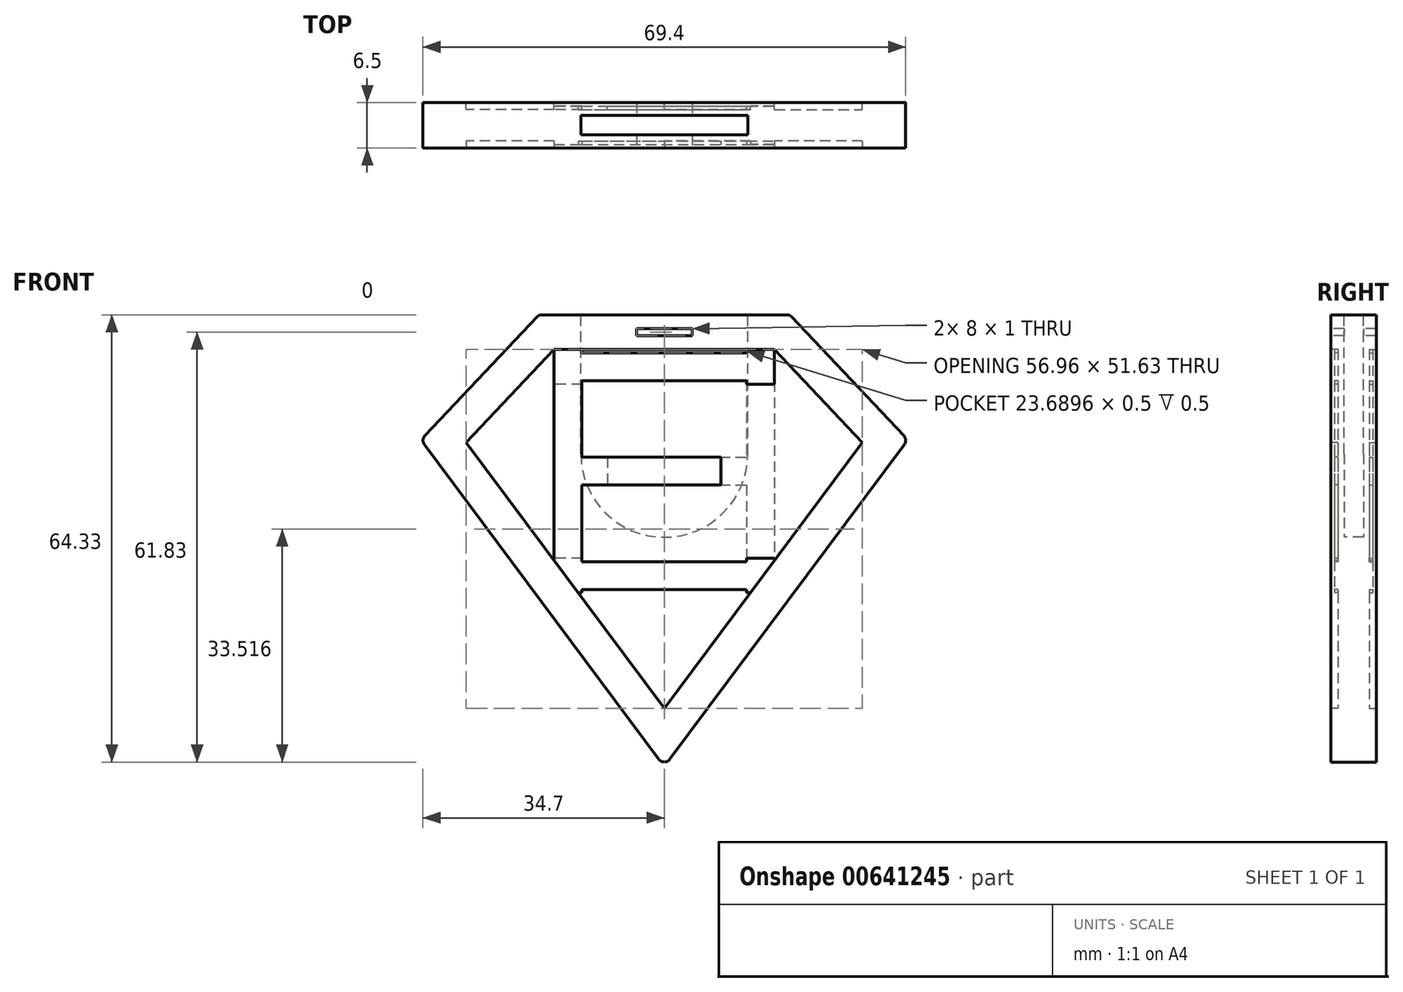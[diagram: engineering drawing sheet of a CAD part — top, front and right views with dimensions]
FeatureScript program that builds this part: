
annotation { "Feature Type Name" : "Feature", "Feature Type Description" : "" }
export const myFeature = defineFeature(function(context is Context, id is Id, definition is map)
    precondition{}
    {
        {
            var Q0;
            Q0=qCreatedBy(makeId("Front.planeOp"),FACE);
            var sketch = newSketch(context, id + "F0", { "sketchPlane" : qUnion([Q0])});
            skLineSegment(sketch, "E0", {"start": v(0, 18) * mm, "end": v(18, 18) * mm});
            skLineSegment(sketch, "E1", {"start": v(18, 18) * mm, "end": v(35, 0) * mm});
            skLineSegment(sketch, "E2", {"start": v(35, 0) * mm, "end": v(0, -47) * mm});
            skLineSegment(sketch, "E3", {"start": v(0, 18) * mm, "end": v(0, -47) * mm, "construction": true});
            skLineSegment(sketch, "E4.MirrorCS", {"start": v(-35, 0) * mm, "end": v(0, -47) * mm});
            skLineSegment(sketch, "E5.MirrorCS", {"start": v(-18, 18) * mm, "end": v(-35, 0) * mm});
            skLineSegment(sketch, "E6.MirrorCS", {"start": v(0, 18) * mm, "end": v(-18, 18) * mm});
            skSolve(sketch);
        }
        {
            var Q0;
            Q0=qSketchRegion(id+"F0",true);
            extrude(context, id + "F1", {"entities" : qUnion([Q0]), "endBound" : BoundingType.SYMMETRIC, "depth" : 6.5 * mm, "offsetDistance" : 25 * mm});
        }
        {
            var Q0;
            Q0=makeQuery(id+"F1.opExtrude","CAP_FACE",FACE,{"disambiguationData":[OSD([sQuery(id+"F0.wireOp",EDGE,"E0"),sQuery(id+"F0.wireOp",EDGE,"E1"),sQuery(id+"F0.wireOp",EDGE,"E2"),sQuery(id+"F0.wireOp",EDGE,"E4.MirrorCS"),sQuery(id+"F0.wireOp",EDGE,"E5.MirrorCS"),sQuery(id+"F0.wireOp",EDGE,"E6.MirrorCS")])],"isStart":false});
            var sketch = newSketch(context, id + "F2", { "sketchPlane" : qUnion([Q0])});
            skLineSegment(sketch, "E7.0", {"start": v(-15.84, 13) * mm, "end": v(15.84, 13) * mm});
            skLineSegment(sketch, "E8.0", {"start": v(-15.84, 13) * mm, "end": v(-28.48, -0.38) * mm});
            skLineSegment(sketch, "E9.0", {"start": v(-28.48, -0.38) * mm, "end": v(0, -38.63) * mm});
            skLineSegment(sketch, "E10.0", {"start": v(28.48, -0.38) * mm, "end": v(0, -38.63) * mm});
            skLineSegment(sketch, "E11.0", {"start": v(15.84, 13) * mm, "end": v(28.48, -0.38) * mm});
            skSolve(sketch);
        }
        {
            var Q0;
            Q0=qSketchRegion(id+"F2",true);
            extrude(context, id + "F3", {"entities" : qUnion([Q0]), "operationType" : NewBodyOperationType.REMOVE, "oppositeDirection" : true, "depth" : 0.5 * mm, "offsetDistance" : 25 * mm});
        }
        {
            var Q0;
            Q0=makeQuery(id+"F1.opExtrude","CAP_FACE",FACE,{"disambiguationData":[OSD([sQuery(id+"F0.wireOp",EDGE,"E0"),sQuery(id+"F0.wireOp",EDGE,"E1"),sQuery(id+"F0.wireOp",EDGE,"E2"),sQuery(id+"F0.wireOp",EDGE,"E4.MirrorCS"),sQuery(id+"F0.wireOp",EDGE,"E5.MirrorCS"),sQuery(id+"F0.wireOp",EDGE,"E6.MirrorCS")])],"isStart":true});
            var sketch = newSketch(context, id + "F4", { "sketchPlane" : qUnion([Q0])});
            skLineSegment(sketch, "E12.0", {"start": v(15.84, 13) * mm, "end": v(-15.84, 13) * mm});
            skLineSegment(sketch, "E13.0", {"start": v(15.84, 13) * mm, "end": v(28.48, -0.38) * mm});
            skLineSegment(sketch, "E14.0", {"start": v(28.48, -0.38) * mm, "end": v(0, -38.63) * mm});
            skLineSegment(sketch, "E15.0", {"start": v(-28.48, -0.38) * mm, "end": v(0, -38.63) * mm});
            skLineSegment(sketch, "E15.1", {"start": v(-15.84, 13) * mm, "end": v(-28.48, -0.38) * mm});
            skSolve(sketch);
        }
        {
            var Q0;
            Q0=qSketchRegion(id+"F4",true);
            extrude(context, id + "F5", {"entities" : qUnion([Q0]), "operationType" : NewBodyOperationType.REMOVE, "oppositeDirection" : true, "depth" : 0.5 * mm, "offsetDistance" : 25 * mm});
        }
        {
            var Q0;
            Q0=makeQuery(id+"F3.boolean.opBoolean","COPY",FACE,{"derivedFrom":makeQuery(id+"F3.opExtrude","CAP_FACE",FACE,{"disambiguationData":[OSD([sQuery(id+"F2.wireOp",EDGE,"E7.0"),sQuery(id+"F2.wireOp",EDGE,"E8.0"),sQuery(id+"F2.wireOp",EDGE,"E9.0"),sQuery(id+"F2.wireOp",EDGE,"E10.0"),sQuery(id+"F2.wireOp",EDGE,"E11.0")])],"isStart":false})});
            var sketch = newSketch(context, id + "F6", { "sketchPlane" : qUnion([Q0])});
            skLineSegment(sketch, "E16", {"start": v(-15.84, 13) * mm, "end": v(-15.84, -17.35) * mm});
            skLineSegment(sketch, "E17", {"start": v(15.84, 13) * mm, "end": v(15.84, 8) * mm});
            skLineSegment(sketch, "E18", {"start": v(-11.84, 8.5) * mm, "end": v(11.84, 8.5) * mm});
            skLineSegment(sketch, "E19", {"start": v(-11.84, -17.5) * mm, "end": v(11.84, -17.5) * mm});
            skLineSegment(sketch, "E20", {"start": v(-11.84, 13) * mm, "end": v(-11.84, 12.5) * mm});
            skLineSegment(sketch, "E21", {"start": v(11.84, 13) * mm, "end": v(11.84, 12.5) * mm});
            skLineSegment(sketch, "E22", {"start": v(11.84, 8) * mm, "end": v(15.84, 8) * mm});
            skLineSegment(sketch, "E23.trimOffspring", {"start": v(11.84, -17) * mm, "end": v(11.84, -17.5) * mm});
            skLineSegment(sketch, "E24.trimOffspring", {"start": v(15.84, -17) * mm, "end": v(15.84, -17.35) * mm});
            skLineSegment(sketch, "E25.trimOffspring", {"start": v(-11.84, 12.5) * mm, "end": v(11.84, 12.5) * mm});
            skLineSegment(sketch, "E26.0", {"start": v(-11.84, 13) * mm, "end": v(11.84, 13) * mm});
            skLineSegment(sketch, "E27.trimOffspring", {"start": v(11.84, 8.5) * mm, "end": v(11.84, 8) * mm});
            skLineSegment(sketch, "E28.trimOffspring", {"start": v(-11.84, 8.5) * mm, "end": v(-11.84, -2.5) * mm});
            skLineSegment(sketch, "E29.0", {"start": v(-12.38, -22) * mm, "end": v(-11.84, -22) * mm});
            skLineSegment(sketch, "E30.trimOffspring", {"start": v(11.84, -17) * mm, "end": v(15.84, -17) * mm});
            skLineSegment(sketch, "E31.trimOffspring", {"start": v(11.84, -22) * mm, "end": v(12.38, -22) * mm});
            skLineSegment(sketch, "E32.trimOffspring", {"start": v(11.84, -21.5) * mm, "end": v(11.84, -22) * mm});
            skLineSegment(sketch, "E33.trimOffspring", {"start": v(-11.84, -21.5) * mm, "end": v(-11.84, -22) * mm});
            skLineSegment(sketch, "E34.trimOffspring", {"start": v(-11.84, -21.5) * mm, "end": v(11.84, -21.5) * mm});
            skLineSegment(sketch, "E35", {"start": v(-11.84, -4.5) * mm, "end": v(8.16, -4.5) * mm, "construction": true});
            skLineSegment(sketch, "E36.0", {"start": v(-11.84, -6.5) * mm, "end": v(8.16, -6.5) * mm});
            skLineSegment(sketch, "E37.0", {"start": v(-11.84, -2.5) * mm, "end": v(8.16, -2.5) * mm});
            skLineSegment(sketch, "E38", {"start": v(8.16, -2.5) * mm, "end": v(8.16, -6.5) * mm});
            skLineSegment(sketch, "E39", {"start": v(-15.84, 13) * mm, "end": v(-28.48, -0.38) * mm});
            skLineSegment(sketch, "E40", {"start": v(-28.48, -0.38) * mm, "end": v(-15.84, -17.35) * mm});
            skLineSegment(sketch, "E41", {"start": v(0, -38.63) * mm, "end": v(12.38, -22) * mm});
            skLineSegment(sketch, "E42", {"start": v(28.48, -0.38) * mm, "end": v(15.84, 13) * mm});
            skLineSegment(sketch, "E43.trimOffspring", {"start": v(15.84, -17.35) * mm, "end": v(28.48, -0.38) * mm});
            skLineSegment(sketch, "E44.trimOffspring", {"start": v(-12.38, -22) * mm, "end": v(0, -38.63) * mm});
            skLineSegment(sketch, "E45.trimOffspring", {"start": v(-11.84, -6.5) * mm, "end": v(-11.84, -17.5) * mm});
            skSolve(sketch);
        }
        {
            var Q0;
            Q0=qSketchRegion(id+"F6",true);
            extrude(context, id + "F7", {"entities" : qUnion([Q0]), "operationType" : NewBodyOperationType.REMOVE, "oppositeDirection" : true, "depth" : 0.5 * mm, "offsetDistance" : 25 * mm});
        }
        {
            var Q0;
            Q0=makeQuery(id+"F5.boolean.opBoolean","COPY",FACE,{"derivedFrom":makeQuery(id+"F5.opExtrude","CAP_FACE",FACE,{"disambiguationData":[OSD([sQuery(id+"F4.wireOp",EDGE,"E12.0"),sQuery(id+"F4.wireOp",EDGE,"E13.0"),sQuery(id+"F4.wireOp",EDGE,"E14.0"),sQuery(id+"F4.wireOp",EDGE,"E15.0"),sQuery(id+"F4.wireOp",EDGE,"E15.1")])],"isStart":false})});
            var sketch = newSketch(context, id + "F8", { "sketchPlane" : qUnion([Q0])});
            skLineSegment(sketch, "E46.0", {"start": v(8.16, -2.5) * mm, "end": v(-11.84, -2.5) * mm});
            skLineSegment(sketch, "E46.1", {"start": v(8.16, -6.5) * mm, "end": v(-11.84, -6.5) * mm});
            skLineSegment(sketch, "E46.2", {"start": v(15.84, 13) * mm, "end": v(15.84, 8) * mm});
            skLineSegment(sketch, "E46.3", {"start": v(11.84, 8.5) * mm, "end": v(11.84, 8) * mm});
            skLineSegment(sketch, "E46.4", {"start": v(-11.84, -21.5) * mm, "end": v(-11.84, -22) * mm});
            skLineSegment(sketch, "E46.5", {"start": v(-11.84, -22) * mm, "end": v(-12.38, -22) * mm});
            skLineSegment(sketch, "E46.6", {"start": v(11.84, -21.5) * mm, "end": v(-11.84, -21.5) * mm});
            skLineSegment(sketch, "E46.7", {"start": v(11.84, -21.5) * mm, "end": v(11.84, -22) * mm});
            skLineSegment(sketch, "E46.8", {"start": v(12.38, -22) * mm, "end": v(11.84, -22) * mm});
            skLineSegment(sketch, "E46.9", {"start": v(11.84, -17.5) * mm, "end": v(-11.84, -17.5) * mm});
            skLineSegment(sketch, "E46.10", {"start": v(-15.84, 13) * mm, "end": v(-15.84, -17.35) * mm});
            skLineSegment(sketch, "E46.11", {"start": v(-11.84, 13) * mm, "end": v(-11.84, 12.5) * mm});
            skLineSegment(sketch, "E46.12", {"start": v(11.84, 12.5) * mm, "end": v(-11.84, 12.5) * mm});
            skLineSegment(sketch, "E46.13", {"start": v(11.84, 13) * mm, "end": v(11.84, 12.5) * mm});
            skLineSegment(sketch, "E46.14", {"start": v(11.84, 8.5) * mm, "end": v(-11.84, 8.5) * mm});
            skLineSegment(sketch, "E46.15", {"start": v(-11.84, 8.5) * mm, "end": v(-11.84, -2.5) * mm});
            skLineSegment(sketch, "E47", {"start": v(11.84, 8) * mm, "end": v(15.84, 8) * mm});
            skLineSegment(sketch, "E48", {"start": v(11.84, -17) * mm, "end": v(15.84, -17) * mm});
            skLineSegment(sketch, "E49", {"start": v(11.84, -17.5) * mm, "end": v(11.84, -17) * mm});
            skLineSegment(sketch, "E50.trimOffspring", {"start": v(15.84, -17) * mm, "end": v(15.84, -17.35) * mm});
            skLineSegment(sketch, "E51", {"start": v(8.16, -2.5) * mm, "end": v(8.16, -6.5) * mm});
            skLineSegment(sketch, "E52.0", {"start": v(-28.48, -0.38) * mm, "end": v(-15.84, -17.35) * mm});
            skLineSegment(sketch, "E52.1", {"start": v(-15.84, 13) * mm, "end": v(-28.48, -0.38) * mm});
            skLineSegment(sketch, "E52.2", {"start": v(11.84, 13) * mm, "end": v(-11.84, 13) * mm});
            skLineSegment(sketch, "E52.3", {"start": v(15.84, 13) * mm, "end": v(28.48, -0.38) * mm});
            skLineSegment(sketch, "E52.4", {"start": v(28.48, -0.38) * mm, "end": v(15.84, -17.35) * mm});
            skLineSegment(sketch, "E53.trimOffspring", {"start": v(-12.38, -22) * mm, "end": v(0, -38.63) * mm});
            skLineSegment(sketch, "E54.trimOffspring", {"start": v(12.38, -22) * mm, "end": v(0, -38.63) * mm});
            skLineSegment(sketch, "E55.trimOffspring", {"start": v(-11.84, -6.5) * mm, "end": v(-11.84, -17.5) * mm});
            skSolve(sketch);
        }
        {
            var Q0;
            Q0=qSketchRegion(id+"F8",true);
            extrude(context, id + "F9", {"entities" : qUnion([Q0]), "operationType" : NewBodyOperationType.REMOVE, "oppositeDirection" : true, "depth" : 0.5 * mm, "offsetDistance" : 25 * mm});
        }
        {
            var Q0;
            Q0=makeQuery(id+"F1.opExtrude","SWEPT_FACE",FACE,{"disambiguationData":[OSD([sQuery(id+"F0.wireOp",EDGE,"E0"),sQuery(id+"F0.wireOp",EDGE,"E6.MirrorCS")])]});
            var sketch = newSketch(context, id + "F10", { "sketchPlane" : qUnion([Q0])});
            skLineSegment(sketch, "E56.bottom", {"start": v(-12, 1.4) * mm, "end": v(12, 1.4) * mm});
            skLineSegment(sketch, "E56.top", {"start": v(-12, -1.4) * mm, "end": v(12, -1.4) * mm});
            skLineSegment(sketch, "E56.left", {"start": v(-12, 1.4) * mm, "end": v(-12, -1.4) * mm});
            skLineSegment(sketch, "E56.right", {"start": v(12, 1.4) * mm, "end": v(12, -1.4) * mm});
            skSolve(sketch);
        }
        {
            var Q0;
            Q0=qSketchRegion(id+"F10",true);
            extrude(context, id + "F11", {"entities" : qUnion([Q0]), "operationType" : NewBodyOperationType.REMOVE, "oppositeDirection" : true, "depth" : 20 * mm, "offsetDistance" : 25 * mm});
        }
        {
            var Q0;
            Q0=qCreatedBy(makeId("Front.planeOp"),FACE);
            var sketch = newSketch(context, id + "F12", { "sketchPlane" : qUnion([Q0])});
            skLineSegment(sketch, "E57.0", {"start": v(-12, -2) * mm, "end": v(12, -2) * mm});
            skArc(sketch, "E58", {"start": v(-12, -2) * mm, "mid": v(0, -14) * mm, "end": v(12, -2) * mm});
            skSolve(sketch);
        }
        {
            var Q0;
            Q0=qSketchRegion(id+"F12",true);
            extrude(context, id + "F13", {"entities" : qUnion([Q0]), "operationType" : NewBodyOperationType.REMOVE, "endBound" : BoundingType.SYMMETRIC, "oppositeDirection" : true, "depth" : 2.8 * mm, "offsetDistance" : 25 * mm});
        }
        {
            var Q0;
            Q0=makeQuery(id+"F1.opExtrude","CAP_FACE",FACE,{"disambiguationData":[OSD([sQuery(id+"F0.wireOp",EDGE,"E0"),sQuery(id+"F0.wireOp",EDGE,"E1"),sQuery(id+"F0.wireOp",EDGE,"E2"),sQuery(id+"F0.wireOp",EDGE,"E4.MirrorCS"),sQuery(id+"F0.wireOp",EDGE,"E5.MirrorCS"),sQuery(id+"F0.wireOp",EDGE,"E6.MirrorCS")])],"isStart":false});
            var sketch = newSketch(context, id + "F14", { "sketchPlane" : qUnion([Q0])});
            skLineSegment(sketch, "E59.bottom", {"start": v(-4, 16) * mm, "end": v(4, 16) * mm});
            skLineSegment(sketch, "E59.top", {"start": v(-4, 15) * mm, "end": v(4, 15) * mm});
            skLineSegment(sketch, "E59.left", {"start": v(-4, 16) * mm, "end": v(-4, 15) * mm});
            skLineSegment(sketch, "E59.right", {"start": v(4, 16) * mm, "end": v(4, 15) * mm});
            skSolve(sketch);
        }
        {
            var Q0;
            Q0=qSketchRegion(id+"F14",true);
            extrude(context, id + "F15", {"entities" : qUnion([Q0]), "operationType" : NewBodyOperationType.REMOVE, "oppositeDirection" : true, "depth" : 25 * mm, "offsetDistance" : 25 * mm});
        }
        {
            var Q0;
            Q0=makeQuery(id+"F1.opExtrude","SWEPT_EDGE",EDGE,{"disambiguationData":[OSD([sQuery(id+"F0.wireOp",EDGE,"E2"),sQuery(id+"F0.wireOp",EDGE,"E4.MirrorCS")])]});
            var Q1;
            Q1=makeQuery(id+"F1.opExtrude","SWEPT_EDGE",EDGE,{"disambiguationData":[OSD([sQuery(id+"F0.wireOp",EDGE,"E1"),sQuery(id+"F0.wireOp",EDGE,"E2")])]});
            var Q2;
            Q2=makeQuery(id+"F1.opExtrude","SWEPT_EDGE",EDGE,{"disambiguationData":[OSD([sQuery(id+"F0.wireOp",EDGE,"E4.MirrorCS"),sQuery(id+"F0.wireOp",EDGE,"E5.MirrorCS")])]});
            var Q3;
            Q3=makeQuery(id+"F1.opExtrude","SWEPT_EDGE",EDGE,{"disambiguationData":[OSD([sQuery(id+"F0.wireOp",EDGE,"E5.MirrorCS"),sQuery(id+"F0.wireOp",EDGE,"E6.MirrorCS")])]});
            var Q4;
            Q4=makeQuery(id+"F1.opExtrude","SWEPT_EDGE",EDGE,{"disambiguationData":[OSD([sQuery(id+"F0.wireOp",EDGE,"E0"),sQuery(id+"F0.wireOp",EDGE,"E1")])]});
            fillet(context, id + "F16", {"entities" : qUnion([Q0, Q1, Q2, Q3, Q4]), "radius" : 1 * mm, "tangentPropagation" : true, "allowEdgeOverflow" : false});
        }
    });
